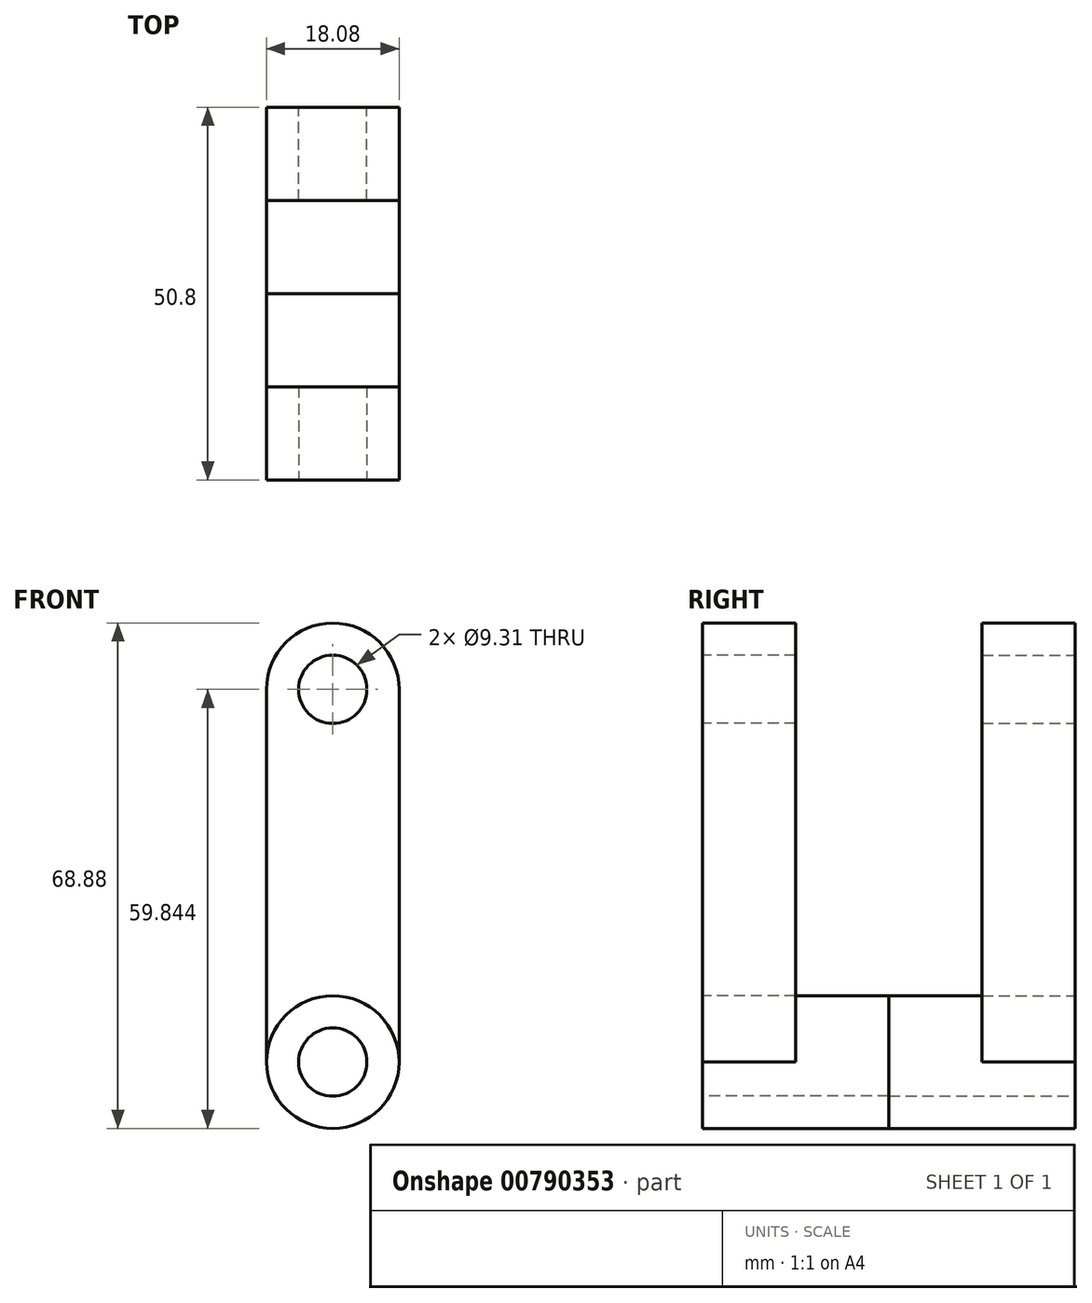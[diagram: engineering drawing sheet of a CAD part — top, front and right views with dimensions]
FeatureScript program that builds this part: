
annotation { "Feature Type Name" : "Feature", "Feature Type Description" : "" }
export const myFeature = defineFeature(function(context is Context, id is Id, definition is map)
    precondition{}
    {
        {
            var Q0;
            Q0=qCreatedBy(makeId("Front.planeOp"),FACE);
            var sketch = newSketch(context, id + "F0", { "sketchPlane" : qUnion([Q0])});
            skLineSegment(sketch, "E0", {"start": v(-9.04, -32.9) * mm, "end": v(-9.04, 17.9) * mm});
            skLineSegment(sketch, "E1", {"start": v(9.04, 17.9) * mm, "end": v(9.04, -32.9) * mm});
            skArc(sketch, "E2", {"start": v(9.04, 17.9) * mm, "mid": v(0, 26.94) * mm, "end": v(-9.04, 17.9) * mm});
            skArc(sketch, "E3", {"start": v(-9.04, -32.9) * mm, "mid": v(0, -41.94) * mm, "end": v(9.04, -32.9) * mm});
            skCircle(sketch, "E4", {"center": v(0, 17.9) * mm, "radius": 4.65 * mm});
            skCircle(sketch, "E5", {"center": v(0, -32.9) * mm, "radius": 4.65 * mm});
            skArc(sketch, "E6", {"start": v(9.04, -32.9) * mm, "mid": v(0, -23.86) * mm, "end": v(-9.04, -32.9) * mm});
            skSolve(sketch);
        }
        {
            var Q0;
            Q0=makeQuery(id+"F0.imprint","IMPRINT",FACE,{"disambiguationData":[TD([[makeQuery(id+"F0.imprint","IMPRINT",EDGE,{"derivedFrom":sQuery(id+"F0.wireOp",EDGE,"E0")}),-1.0]])]});
            extrude(context, id + "F1", {"entities" : qUnion([Q0]), "oppositeDirection" : true, "depth" : 12.7 * mm, "offsetDistance" : 25.4 * mm});
        }
        {
            var Q0;
            Q0=makeQuery(id+"F0.imprint","IMPRINT",FACE,{"disambiguationData":[TD([[makeQuery(id+"F0.imprint","IMPRINT",EDGE,{"derivedFrom":sQuery(id+"F0.wireOp",EDGE,"E3")}),1.0]])]});
            extrude(context, id + "F2", {"entities" : qUnion([Q0]), "oppositeDirection" : true, "depth" : 25.4 * mm, "offsetDistance" : 25.4 * mm});
        }
        {
            var Q0;
            Q0=makeQuery(id+"F1.opExtrude","SWEPT_BODY",BODY,{"disambiguationData":[OSD([sQuery(id+"F0.wireOp",EDGE,"E0"),sQuery(id+"F0.wireOp",EDGE,"E1"),sQuery(id+"F0.wireOp",EDGE,"E2"),sQuery(id+"F0.wireOp",EDGE,"E4"),sQuery(id+"F0.wireOp",EDGE,"E6")])]});
            var Q1;
            Q1=makeQuery(id+"F2.opExtrude","SWEPT_BODY",BODY,{"disambiguationData":[OSD([sQuery(id+"F0.wireOp",EDGE,"E3"),sQuery(id+"F0.wireOp",EDGE,"E5"),sQuery(id+"F0.wireOp",EDGE,"E6")])]});
            var Q2;
            Q2=makeQuery(id+"F2.opExtrude","CAP_FACE",FACE,{"disambiguationData":[OSD([sQuery(id+"F0.wireOp",EDGE,"E3"),sQuery(id+"F0.wireOp",EDGE,"E5"),sQuery(id+"F0.wireOp",EDGE,"E6")])],"isStart":false});
            mirror(context, id + "F3", {"entities" : qUnion([Q0, Q1]), "mirrorPlane" : qUnion([Q2])});
        }
    });
